# Revit family: 1SE_Trez_TC_2C_2500_With_Pit
name_source: partatom
category: Specialty Equipment
units: mm (PartAtom-declared; Revit-internal decimal feet)

## family parameters
Always vertical = Yes
Cut with Voids When Loaded = Yes
Part Type = Normal
Room Calculation Point = No
Round Connector Dimension = Use Diameter
Shared = No
Work Plane-Based = No

## types (1)
- Platform-2300x2300mm with Door Height 2500mm
    Cabin = Speciality_Equipment_Trez_Cabin : Cabin
    Cabin or Platform = Speciality_Equipment_Trez_Platform : Platform
    Cabin or Platform Back = No
    Clear Depth = 2300 mm
    Clear Width = 2300 mm
    Clearance = 370 mm  [stored 1.21391 ft]
    Description = Hydraulic goods only lift with two cylinders.
    Door Clear Height = 2500 mm  [stored 8.2021 ft]
    Door Clear Width = 2300 mm
    Headroom = 3100 mm  [stored 10.1706 ft]
    Manufacturer = TREZ Ltd.
    Model = TC 2C 2500
    Pit Height = 250 mm  [stored 0.82021 ft]
    Platform = Speciality_Equipment_Trez_Platform : Platform
    Platform Material = TREZ_Steel
    Profiles Material = TREZ_Steel
    Rail Height = 7850 mm  [stored 25.7546 ft]
    Real Depth = 2300 mm
    Real Width = 2300 mm
    Safe Space = 600 mm
    Safe Working Load = 2500.00 kg
    Shaft = TREZ_Shaft_Space
    Shaft Depth = 2400 mm
    Shaft Width = 3040 mm
    Tower Cladding Material = TREZ_Steel_Cladding
    Travel = 4500 mm
    URL = https://trez.bg

note: [stored X ft] marks values corroborated as IEEE doubles in the binary element streams (Revit-internal decimal feet)

## geometry (parser evidence)
native form markers: Sweep x13
no freeform markers — native parametric forms only
